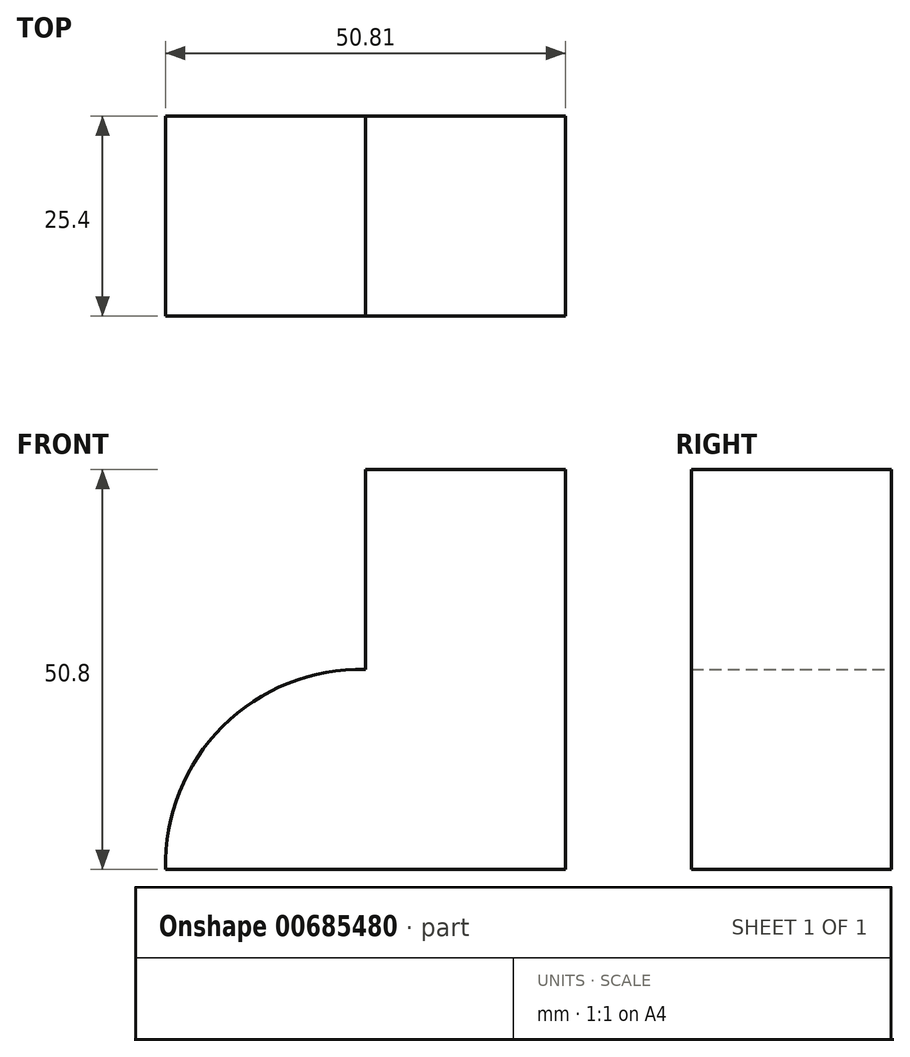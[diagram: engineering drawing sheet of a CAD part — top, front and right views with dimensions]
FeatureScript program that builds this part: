
annotation { "Feature Type Name" : "Feature", "Feature Type Description" : "" }
export const myFeature = defineFeature(function(context is Context, id is Id, definition is map)
    precondition{}
    {
        {
            var Q0;
            Q0=qCreatedBy(makeId("Front.planeOp"),FACE);
            var sketch = newSketch(context, id + "F0", { "sketchPlane" : qUnion([Q0])});
            skLineSegment(sketch, "E0", {"start": v(0, 0) * mm, "end": v(0, 50.8) * mm});
            skLineSegment(sketch, "E1", {"start": v(0, 50.8) * mm, "end": v(-25.4, 50.8) * mm});
            skLineSegment(sketch, "E2", {"start": v(-25.4, 50.8) * mm, "end": v(-25.4, 25.4) * mm});
            skLineSegment(sketch, "E3", {"start": v(0, 0) * mm, "end": v(-50.8, 0) * mm});
            skArc(sketch, "E4", {"start": v(-25.4, 25.4) * mm, "mid": v(-43.55, 18.15) * mm, "end": v(-50.8, 0) * mm});
            skSolve(sketch);
        }
        {
            var Q0;
            Q0 = qSketchRegion(id + "F0", true);
            extrude(context, id + "F1", {"entities" : qUnion([Q0]), "depth" : 25.4 * mm, "offsetDistance" : 25.4 * mm});
        }
    });
